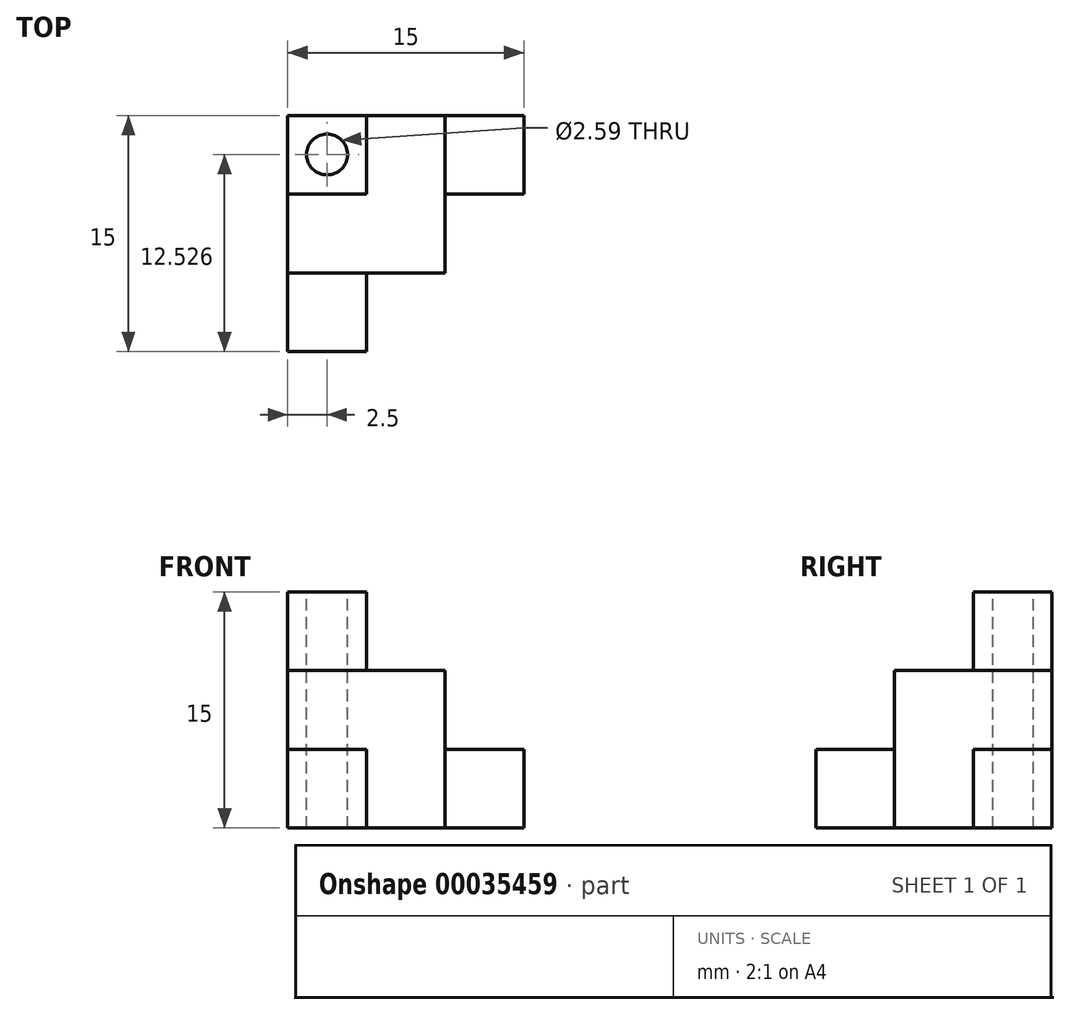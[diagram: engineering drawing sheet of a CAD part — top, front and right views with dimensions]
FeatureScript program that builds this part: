
annotation { "Feature Type Name" : "Feature", "Feature Type Description" : "" }
export const myFeature = defineFeature(function(context is Context, id is Id, definition is map)
    precondition{}
    {
        {
            var Q0;
            Q0=qCreatedBy(makeId("Top.planeOp"),FACE);
            var sketch = newSketch(context, id + "F0", { "sketchPlane" : qUnion([Q0])});
            skLineSegment(sketch, "E0.bottom", {"start": v(-10, 10) * mm, "end": v(0, 10) * mm});
            skLineSegment(sketch, "E0.top", {"start": v(-10, 0) * mm, "end": v(0, 0) * mm});
            skLineSegment(sketch, "E0.left", {"start": v(-10, 10) * mm, "end": v(-10, 0) * mm});
            skLineSegment(sketch, "E0.right", {"start": v(0, 10) * mm, "end": v(0, 0) * mm});
            skSolve(sketch);
        }
        {
            var Q0;
            Q0=makeQuery(id+"F0.imprint","IMPRINT",FACE,{"disambiguationData":[TD([[makeQuery(id+"F0.imprint","IMPRINT",EDGE,{"derivedFrom":sQuery(id+"F0.wireOp",EDGE,"E0.bottom")}),-1.0]])]});
            extrude(context, id + "F1", {"entities" : qUnion([Q0]), "depth" : 10 * mm});
        }
        {
            var Q0;
            Q0=makeQuery(id+"F1.opExtrude","SWEPT_FACE",FACE,{"disambiguationData":[OSD([sQuery(id+"F0.wireOp",EDGE,"E0.right")])]});
            var sketch = newSketch(context, id + "F2", { "sketchPlane" : qUnion([Q0])});
            skPoint(sketch, "E1.oppositeSnap0", {"position": v(10, 5) * mm});
            skPoint(sketch, "E1.oppositeSnap1", {"position": v(5, 0) * mm});
            skLineSegment(sketch, "E1.bottom", {"start": v(10, 0) * mm, "end": v(5, 0) * mm});
            skLineSegment(sketch, "E1.top", {"start": v(10, 5) * mm, "end": v(5, 5) * mm});
            skLineSegment(sketch, "E1.left", {"start": v(10, 0) * mm, "end": v(10, 5) * mm});
            skLineSegment(sketch, "E1.right", {"start": v(5, 0) * mm, "end": v(5, 5) * mm});
            skSolve(sketch);
        }
        {
            var Q0;
            Q0=makeQuery(id+"F2.imprint","IMPRINT",FACE,{"disambiguationData":[TD([[makeQuery(id+"F2.imprint","IMPRINT",EDGE,{"derivedFrom":sQuery(id+"F2.wireOp",EDGE,"E1.bottom")}),-1.0]])]});
            extrude(context, id + "F3", {"entities" : qUnion([Q0]), "operationType" : NewBodyOperationType.ADD, "depth" : 5 * mm});
        }
        {
            var Q0;
            Q0=makeQuery(id+"F1.opExtrude","SWEPT_FACE",FACE,{"disambiguationData":[OSD([sQuery(id+"F0.wireOp",EDGE,"E0.top")])]});
            var sketch = newSketch(context, id + "F4", { "sketchPlane" : qUnion([Q0])});
            skPoint(sketch, "E2.oppositeSnap0", {"position": v(-10, 5) * mm});
            skPoint(sketch, "E2.oppositeSnap1", {"position": v(-5, 0) * mm});
            skLineSegment(sketch, "E2.bottom", {"start": v(-10, 0) * mm, "end": v(-5, 0) * mm});
            skLineSegment(sketch, "E2.top", {"start": v(-10, 5) * mm, "end": v(-5, 5) * mm});
            skLineSegment(sketch, "E2.left", {"start": v(-10, 0) * mm, "end": v(-10, 5) * mm});
            skLineSegment(sketch, "E2.right", {"start": v(-5, 0) * mm, "end": v(-5, 5) * mm});
            skSolve(sketch);
        }
        {
            var Q0;
            Q0=makeQuery(id+"F4.imprint","IMPRINT",FACE,{"disambiguationData":[TD([[makeQuery(id+"F4.imprint","IMPRINT",EDGE,{"derivedFrom":sQuery(id+"F4.wireOp",EDGE,"E2.bottom")}),1.0]])]});
            extrude(context, id + "F5", {"entities" : qUnion([Q0]), "operationType" : NewBodyOperationType.ADD, "depth" : 5 * mm});
        }
        {
            var Q0;
            Q0=makeQuery(id+"F1.opExtrude","CAP_FACE",FACE,{"disambiguationData":[OSD([sQuery(id+"F0.wireOp",EDGE,"E0.bottom"),sQuery(id+"F0.wireOp",EDGE,"E0.top"),sQuery(id+"F0.wireOp",EDGE,"E0.left"),sQuery(id+"F0.wireOp",EDGE,"E0.right")])],"isStart":false});
            var sketch = newSketch(context, id + "F6", { "sketchPlane" : qUnion([Q0])});
            skPoint(sketch, "E3.oppositeSnap0", {"position": v(-10, 5) * mm});
            skPoint(sketch, "E3.oppositeSnap1", {"position": v(-5, 10) * mm});
            skLineSegment(sketch, "E3.bottom", {"start": v(-10, 10) * mm, "end": v(-5, 10) * mm});
            skLineSegment(sketch, "E3.top", {"start": v(-10, 5) * mm, "end": v(-5, 5) * mm});
            skLineSegment(sketch, "E3.left", {"start": v(-10, 10) * mm, "end": v(-10, 5) * mm});
            skLineSegment(sketch, "E3.right", {"start": v(-5, 10) * mm, "end": v(-5, 5) * mm});
            skSolve(sketch);
        }
        {
            var Q0;
            Q0=makeQuery(id+"F6.imprint","IMPRINT",FACE,{"disambiguationData":[TD([[makeQuery(id+"F6.imprint","IMPRINT",EDGE,{"derivedFrom":sQuery(id+"F6.wireOp",EDGE,"E3.bottom")}),-1.0]])]});
            extrude(context, id + "F7", {"entities" : qUnion([Q0]), "operationType" : NewBodyOperationType.ADD, "depth" : 5 * mm});
        }
        {
            var Q0;
            Q0=makeQuery(id+"F7.opExtrude","CAP_FACE",FACE,{"disambiguationData":[OSD([sQuery(id+"F6.wireOp",EDGE,"E3.bottom"),sQuery(id+"F6.wireOp",EDGE,"E3.top"),sQuery(id+"F6.wireOp",EDGE,"E3.left"),sQuery(id+"F6.wireOp",EDGE,"E3.right")])],"isStart":false});
            var sketch = newSketch(context, id + "F8", { "sketchPlane" : qUnion([Q0])});
            skCircle(sketch, "E4", {"center": v(-7.5, 7.53) * mm, "radius": 1.3 * mm});
            skPoint(sketch, "E4.centerSnap0", {"position": v(-7.5, 10) * mm});
            skSolve(sketch);
        }
        {
            var Q0;
            Q0=makeQuery(id+"F8.imprint","IMPRINT",FACE,{"disambiguationData":[TD([[makeQuery(id+"F8.imprint","IMPRINT",EDGE,{"derivedFrom":sQuery(id+"F8.wireOp",EDGE,"E4")}),1.0]])]});
            extrude(context, id + "F9", {"entities" : qUnion([Q0]), "operationType" : NewBodyOperationType.REMOVE, "oppositeDirection" : true, "depth" : 25 * mm});
        }
    });
